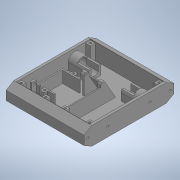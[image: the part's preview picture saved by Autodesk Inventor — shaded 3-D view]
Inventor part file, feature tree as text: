
AUTODESK INVENTOR PART (.ipt)
format: ipt  version: 2020 (Build 240168000, 168)  size: 647,168 bytes
history: native  units: in
note: dims shown in document units (in); Inventor stores cm internally (conversion verified against a paired STEP export)
features: extrude x19, sketch x19, projected_geometry x14, mirror x6, plane x1
ambient origin geometry x8: Origin, YZ Plane, XZ Plane, XY Plane, X Axis, Y Axis, Z Axis, Center Point
bodies: Solid1 (feature_tree)
feature tree (59):
  extrude  "Extrusion1"  Depth=5.9055in
  extrude  "Extrusion2"  TaperAngle=0.0deg  [1 undecoded]
  extrude  "Extrusion3"  Depth=1.063in
  extrude  "Extrusion4"  Depth=0.315in
  extrude  "Extrusion5"  TaperAngle=0.0deg  [1 undecoded]
  extrude  "Extrusion6"  Depth=0.5906in
  mirror  "Mirror1"
  extrude  "Extrusion7"  Depth=0.0787in
  mirror  "Mirror2"
  extrude  "Extrusion8"  Depth=0.6102in
  mirror  "Mirror3"
  plane  "Work Plane1"
  extrude  "Extrusion9"  Depth=0.7874in TaperAngle=0.0deg
  mirror  "Mirror4"
  extrude  "Extrusion10"  Depth=6.063in TaperAngle=0.0deg
  extrude  "Extrusion11"  Depth=0.1575in
  extrude  "Extrusion12"  TaperAngle=0.0deg  [1 undecoded]
  extrude  "Extrusion13"  Depth=0.2756in
  extrude  "Extrusion14"  Depth=0.4331in
  extrude  "Extrusion17"  Depth=2.7559in
  extrude  "Extrusion18"  Depth=0.0492in
  mirror  "Mirror6"
  extrude  "Extrusion19"  TaperAngle=0.0deg  [1 undecoded]
  mirror  "Mirror7"
  extrude  "Extrusion20"  Depth=0.0787in
  extrude  "Extrusion21"  Depth=0.993in
  sketch  "Sketch1"  dims[d0=1.1811in d1=5.9055in]
  sketch  "Sketch2"  dims[d2=5.1181in d3=0.0in]
  projected_geometry  "Projected Loop1"
  sketch  "Sketch3"  dims[d4=0.1575in d5=1.063in]
  projected_geometry  "Projected Loop2"
  projected_geometry  "Projected Loop3"
  sketch  "Sketch4"  dims[d6=0.0in d8=0.315in]
  sketch  "Sketch5"  dims[d10=0.993in d11=0.0in]
  projected_geometry  "Projected Loop4"
  sketch  "Sketch6"  dims[d12=0.6496in d13=0.5906in]
  sketch  "Sketch7"  dims[d14=1.5748in d15=0.0787in]
  sketch  "Sketch9"  dims[d16=0.5512in d17=0.0in d18=0.6102in]
  sketch  "Sketch10"  dims[d19=0.4803in d20=0.7874in d21=0.0in]
  sketch  "Sketch12"  dims[d22=0.1654in d23=6.063in d24=0.0in]
  projected_geometry  "Projected Loop6"
  projected_geometry  "Projected Loop7"
  projected_geometry  "Projected Loop8"
  sketch  "Sketch13"  dims[d25=0.5114in d26=0.1575in]
  sketch  "Sketch14"  dims[d27=1.5748in d28=0.0in d29=0.0in]
  sketch  "Sketch15"  dims[d30=0.1575in d31=0.2756in]
  projected_geometry  "Projected Loop15"
  sketch  "Sketch16"  dims[d32=0.0in d33=0.4331in]
  projected_geometry  "Projected Loop19"
  projected_geometry  "Projected Loop20"
  projected_geometry  "Projected Loop21"
  projected_geometry  "Projected Loop22"
  projected_geometry  "Projected Loop23"
  projected_geometry  "Projected Loop24"
  sketch  "Sketch20"  dims[d34=0.0984in d38=2.7559in]
  sketch  "Sketch21"  dims[d40=0.0492in d41=0.0909in]
  sketch  "Sketch22"  dims[d42=0.2362in d43=0.0in]
  sketch  "Sketch23"  dims[d44=60.0deg d45=0.0787in]
  sketch  "Sketch25"  dims[d46=0.315in d48=0.993in d49=0.0in d53=0.2756in d54=0.0in d55=0.4724in d56=1.1811in d57=1.5748in d58=1.5748in d59=0.0787in d60=0.0787in d62=0.315in d63=0.7677in d64=0.0in d66=0.1476in d67=0.2756in d68=0.0in d69=0.7874in d70=0.2953in d71=0.1181in d72=0.0in d89=0.0157in d90=0.0157in d91=0.1476in d92=0.1476in d96=0.315in d97=0.1575in d98=0.1181in d99=0.0in d102=0.1772in d104=0.3346in d105=135.0deg d106=0.2362in d107=0.0in d108=0.0394in d109=0.0in d110=0.063in d111=0.0394in d112=0.0in d117=0.993in d118=0.063in d119=0.3937in d120=0.0in]
note: 4 required parameter values undecoded (feature->parameter linkage not recoverable at this tier; creation-order binding heuristic only, values carry confidence <= 0.55)
